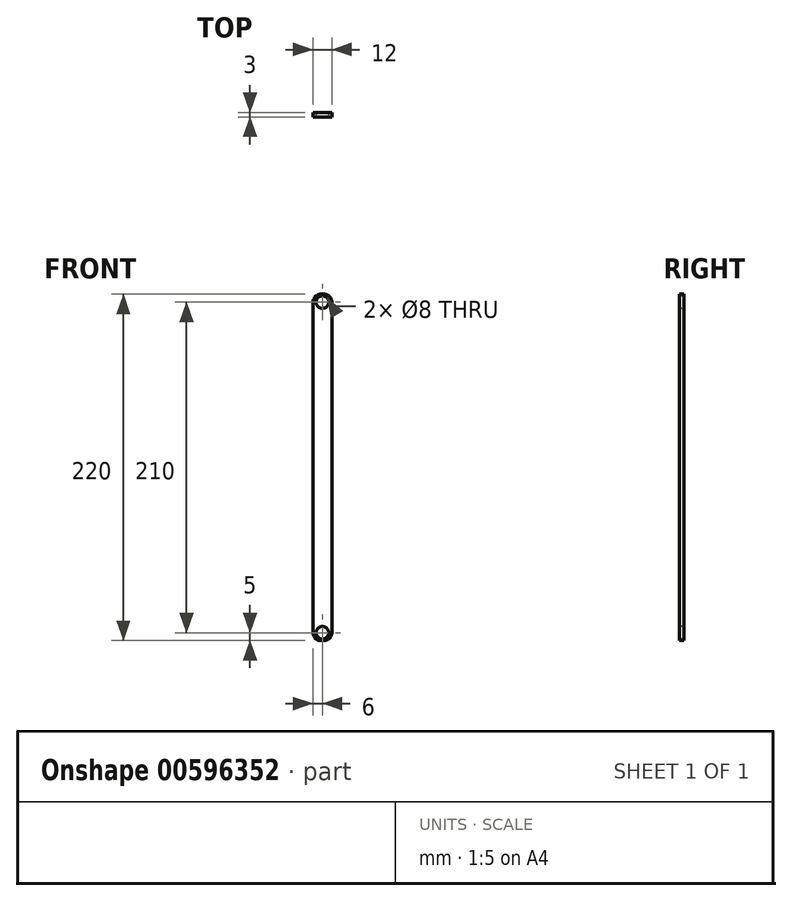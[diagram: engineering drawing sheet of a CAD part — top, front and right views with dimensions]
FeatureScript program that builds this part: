
annotation { "Feature Type Name" : "Feature", "Feature Type Description" : "" }
export const myFeature = defineFeature(function(context is Context, id is Id, definition is map)
    precondition{}
    {
        {
            var Q0;
            Q0=qCreatedBy(makeId("Front.planeOp"),FACE);
            var sketch = newSketch(context, id + "F0", { "sketchPlane" : qUnion([Q0])});
            skLineSegment(sketch, "E0.bottom", {"start": v(0, 0) * mm, "end": v(12, 0) * mm});
            skLineSegment(sketch, "E0.top", {"start": v(0, 220) * mm, "end": v(12, 220) * mm});
            skLineSegment(sketch, "E0.left", {"start": v(0, 0) * mm, "end": v(0, 220) * mm});
            skLineSegment(sketch, "E0.right", {"start": v(12, 0) * mm, "end": v(12, 220) * mm});
            skSolve(sketch);
        }
        {
            var Q0;
            Q0=makeQuery(id+"F0.imprint","IMPRINT",FACE,{"disambiguationData":[TD([[makeQuery(id+"F0.imprint","IMPRINT",EDGE,{"derivedFrom":sQuery(id+"F0.wireOp",EDGE,"E0.bottom")}),1.0]])]});
            extrude(context, id + "F1", {"entities" : qUnion([Q0]), "depth" : 3 * mm, "offsetDistance" : 25 * mm});
        }
        {
            var Q0;
            Q0=makeQuery(id+"F1.opExtrude","SWEPT_EDGE",EDGE,{"disambiguationData":[OSD([sQuery(id+"F0.wireOp",EDGE,"E0.top"),sQuery(id+"F0.wireOp",EDGE,"E0.left")])]});
            fillet(context, id + "F2", {"entities" : qUnion([Q0]), "radius" : 5 * mm, "tangentPropagation" : true, "allowEdgeOverflow" : false});
        }
        {
            var Q0;
            Q0=makeQuery(id+"F1.opExtrude","SWEPT_EDGE",EDGE,{"disambiguationData":[OSD([sQuery(id+"F0.wireOp",EDGE,"E0.top"),sQuery(id+"F0.wireOp",EDGE,"E0.right")])]});
            fillet(context, id + "F3", {"entities" : qUnion([Q0]), "radius" : 5 * mm, "tangentPropagation" : true, "allowEdgeOverflow" : false});
        }
        {
            var Q0;
            Q0=makeQuery(id+"F1.opExtrude","SWEPT_EDGE",EDGE,{"disambiguationData":[OSD([sQuery(id+"F0.wireOp",EDGE,"E0.bottom"),sQuery(id+"F0.wireOp",EDGE,"E0.left")])]});
            fillet(context, id + "F4", {"entities" : qUnion([Q0]), "radius" : 5 * mm, "tangentPropagation" : true, "allowEdgeOverflow" : false});
        }
        {
            var Q0;
            Q0=makeQuery(id+"F1.opExtrude","SWEPT_EDGE",EDGE,{"disambiguationData":[OSD([sQuery(id+"F0.wireOp",EDGE,"E0.bottom"),sQuery(id+"F0.wireOp",EDGE,"E0.right")])]});
            fillet(context, id + "F5", {"entities" : qUnion([Q0]), "radius" : 5 * mm, "tangentPropagation" : true, "allowEdgeOverflow" : false});
        }
        {
            var Q0;
            Q0=makeQuery(id+"F1.opExtrude","CAP_FACE",FACE,{"disambiguationData":[OSD([sQuery(id+"F0.wireOp",EDGE,"E0.bottom"),sQuery(id+"F0.wireOp",EDGE,"E0.top"),sQuery(id+"F0.wireOp",EDGE,"E0.left"),sQuery(id+"F0.wireOp",EDGE,"E0.right")])],"isStart":false});
            var sketch = newSketch(context, id + "F6", { "sketchPlane" : qUnion([Q0])});
            skLineSegment(sketch, "E1.0.0", {"start": v(5, 0) * mm, "end": v(7, 0) * mm});
            skArc(sketch, "E1.0.1", {"start": v(7, 0) * mm, "mid": v(10.54, 1.46) * mm, "end": v(12, 5) * mm});
            skLineSegment(sketch, "E1.0.2", {"start": v(12, 5) * mm, "end": v(12, 215) * mm});
            skArc(sketch, "E1.0.3", {"start": v(12, 215) * mm, "mid": v(10.54, 218.54) * mm, "end": v(7, 220) * mm});
            skLineSegment(sketch, "E1.0.4", {"start": v(7, 220) * mm, "end": v(5, 220) * mm});
            skArc(sketch, "E1.0.5", {"start": v(5, 220) * mm, "mid": v(1.46, 218.54) * mm, "end": v(0, 215) * mm});
            skLineSegment(sketch, "E1.0.6", {"start": v(0, 215) * mm, "end": v(0, 5) * mm});
            skArc(sketch, "E1.0.7", {"start": v(0, 5) * mm, "mid": v(1.46, 1.46) * mm, "end": v(5, 0) * mm});
            skLineSegment(sketch, "E2", {"start": v(5, 5) * mm, "end": v(7, 5) * mm});
            skLineSegment(sketch, "E3", {"start": v(7, 5) * mm, "end": v(6, 5) * mm});
            skCircle(sketch, "E4", {"center": v(6, 5) * mm, "radius": 4 * mm});
            skLineSegment(sketch, "E5", {"start": v(5, 215) * mm, "end": v(7, 215) * mm});
            skLineSegment(sketch, "E6", {"start": v(6, 215) * mm, "end": v(7, 215) * mm});
            skCircle(sketch, "E7", {"center": v(6, 215) * mm, "radius": 4 * mm});
            skSolve(sketch);
        }
        {
            var Q0;
            Q0=makeQuery(id+"F6.imprint","IMPRINT",FACE,{"disambiguationData":[TD([[makeQuery(id+"F6.imprint","IMPRINT",EDGE,{"derivedFrom":sQuery(id+"F6.wireOp",EDGE,"E7")}),1.0]])]});
            var Q1;
            Q1=makeQuery(id+"F6.imprint","IMPRINT",FACE,{"disambiguationData":[TD([[makeQuery(id+"F6.imprint","IMPRINT",EDGE,{"derivedFrom":sQuery(id+"F6.wireOp",EDGE,"E4")}),1.0]])]});
            extrude(context, id + "F7", {"entities" : qUnion([Q0, Q1]), "operationType" : NewBodyOperationType.REMOVE, "oppositeDirection" : true, "depth" : 25 * mm, "offsetDistance" : 25 * mm});
        }
    });
